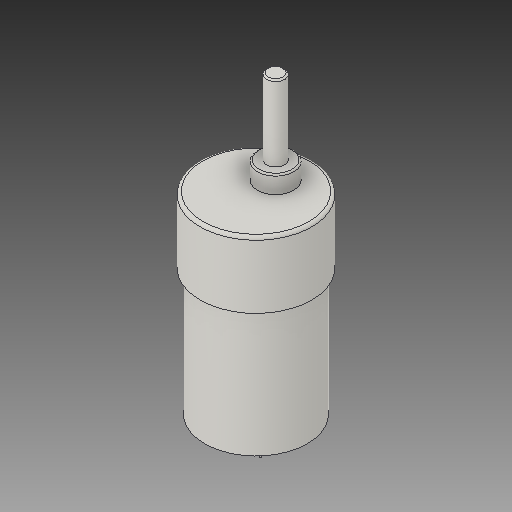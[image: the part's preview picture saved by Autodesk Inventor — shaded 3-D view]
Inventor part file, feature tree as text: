
AUTODESK INVENTOR PART (.ipt)
format: ipt  version: 2017 (Build 210142000, 142)  size: 211,968 bytes
history: native  units: in
note: dims shown in document units (in); Inventor stores cm internally (conversion verified against a paired STEP export)
features: fillet x1
ambient origin geometry x8: Origin, YZ Plane, XZ Plane, XY Plane, X Axis, Y Axis, Z Axis, Center Point
bodies: Solid1 (feature_tree)
feature tree (1):
  fillet  "Fillet2"  [1 undecoded]
note: 1 required parameter value undecoded (feature->parameter linkage not recoverable at this tier; creation-order binding heuristic only, values carry confidence <= 0.55)
